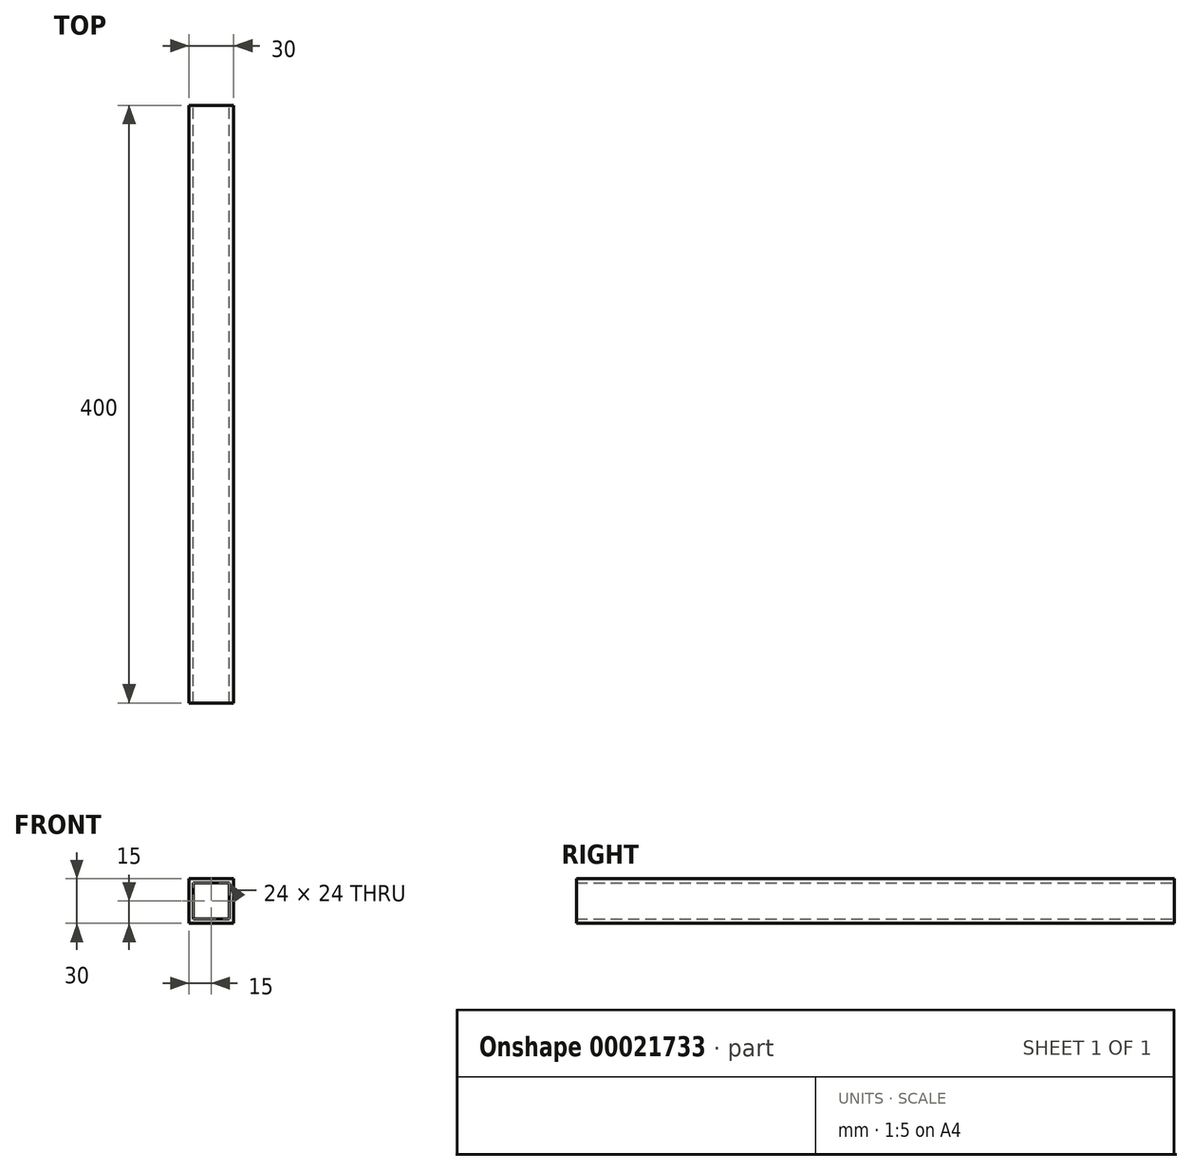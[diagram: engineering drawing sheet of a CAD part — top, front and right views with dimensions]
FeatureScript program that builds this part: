
annotation { "Feature Type Name" : "Feature", "Feature Type Description" : "" }
export const myFeature = defineFeature(function(context is Context, id is Id, definition is map)
    precondition{}
    {
        {
            var Q0;
            Q0=qCreatedBy(makeId("Front.planeOp"),FACE);
            var sketch = newSketch(context, id + "F0", { "sketchPlane" : qUnion([Q0])});
            skLineSegment(sketch, "E0.bottom", {"start": v(-15, 15) * mm, "end": v(15, 15) * mm});
            skLineSegment(sketch, "E0.top", {"start": v(-15, -15) * mm, "end": v(15, -15) * mm});
            skLineSegment(sketch, "E0.left", {"start": v(-15, 15) * mm, "end": v(-15, -15) * mm});
            skLineSegment(sketch, "E0.right", {"start": v(15, 15) * mm, "end": v(15, -15) * mm});
            skLineSegment(sketch, "E1.bottom", {"start": v(-12, 12) * mm, "end": v(12, 12) * mm});
            skLineSegment(sketch, "E1.top", {"start": v(-12, -12) * mm, "end": v(12, -12) * mm});
            skLineSegment(sketch, "E1.left", {"start": v(-12, 12) * mm, "end": v(-12, -12) * mm});
            skLineSegment(sketch, "E1.right", {"start": v(12, 12) * mm, "end": v(12, -12) * mm});
            skSolve(sketch);
        }
        {
            var Q0;
            Q0=makeQuery(id+"F0.imprint","IMPRINT",FACE,{"disambiguationData":[TD([[makeQuery(id+"F0.imprint","IMPRINT",EDGE,{"derivedFrom":sQuery(id+"F0.wireOp",EDGE,"E0.bottom")}),-1.0]])]});
            extrude(context, id + "F1", {"entities" : qUnion([Q0]), "depth" : 400 * mm});
        }
    });
